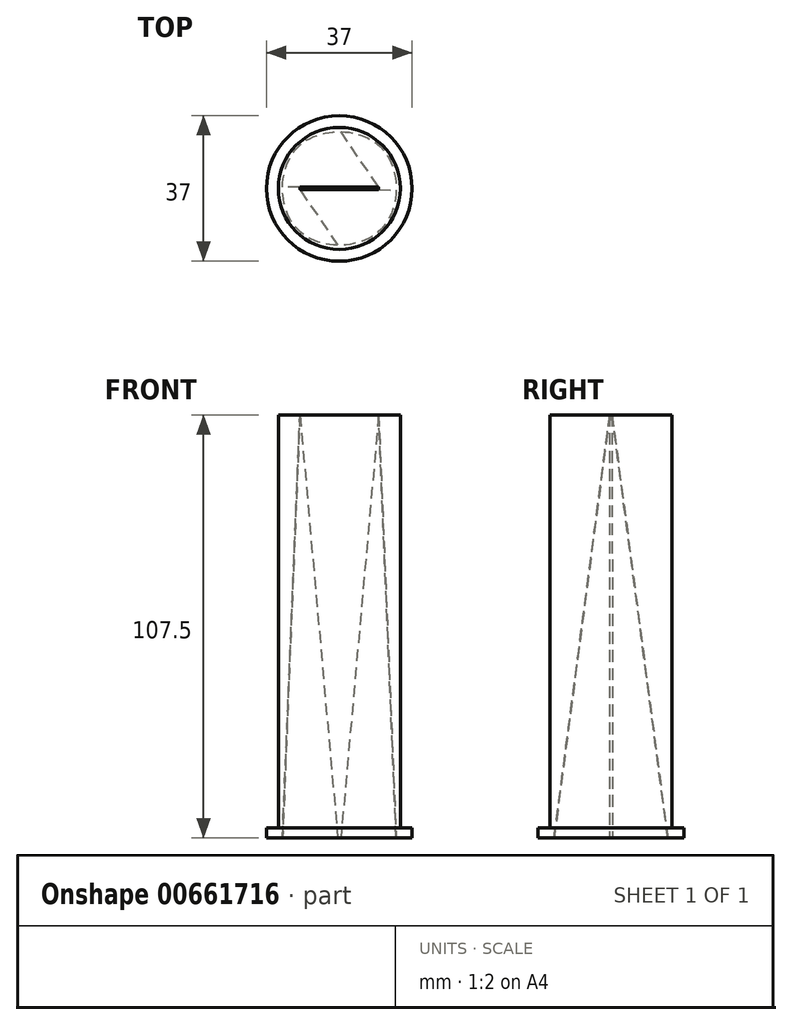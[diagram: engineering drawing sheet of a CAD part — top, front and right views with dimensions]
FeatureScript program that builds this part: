
annotation { "Feature Type Name" : "Feature", "Feature Type Description" : "" }
export const myFeature = defineFeature(function(context is Context, id is Id, definition is map)
    precondition{}
    {
        {
            var Q0;
            Q0=qCreatedBy(makeId("Top.planeOp"),FACE);
            var sketch = newSketch(context, id + "F0", { "sketchPlane" : qUnion([Q0])});
            skCircle(sketch, "E0", {"center": v(0, 0) * mm, "radius": 18.5 * mm});
            skSolve(sketch);
        }
        {
            var Q0;
            Q0=makeQuery(id+"F0.imprint","IMPRINT",FACE,{"disambiguationData":[TD([[makeQuery(id+"F0.imprint","IMPRINT",EDGE,{"derivedFrom":sQuery(id+"F0.wireOp",EDGE,"E0")}),1.0]])]});
            extrude(context, id + "F1", {"entities" : qUnion([Q0]), "depth" : 2.5 * mm, "offsetDistance" : 25 * mm});
        }
        {
            var Q0;
            Q0=makeQuery(id+"F1.opExtrude","CAP_FACE",FACE,{"disambiguationData":[OSD([sQuery(id+"F0.wireOp",EDGE,"E0")])],"isStart":false});
            var sketch = newSketch(context, id + "F2", { "sketchPlane" : qUnion([Q0])});
            skCircle(sketch, "E1", {"center": v(0, 0) * mm, "radius": 15.5 * mm});
            skSolve(sketch);
        }
        {
            var Q0;
            Q0 = qSketchRegion(id + "F2", true);
            extrude(context, id + "F3", {"entities" : qUnion([Q0]), "operationType" : NewBodyOperationType.ADD, "depth" : 105 * mm, "offsetDistance" : 25 * mm});
        }
        {
            var Q0;
            Q0=makeQuery(id+"F3.opExtrude","CAP_FACE",FACE,{"disambiguationData":[OSD([sQuery(id+"F2.wireOp",EDGE,"E1")])],"isStart":false});
            var sketch = newSketch(context, id + "F4", { "sketchPlane" : qUnion([Q0])});
            skLineSegment(sketch, "E2.bottom", {"start": v(-10, 0.3) * mm, "end": v(10, 0.3) * mm});
            skLineSegment(sketch, "E2.top", {"start": v(-10, -0.3) * mm, "end": v(10, -0.3) * mm});
            skLineSegment(sketch, "E2.left", {"start": v(-10, 0.3) * mm, "end": v(-10, -0.3) * mm});
            skLineSegment(sketch, "E2.right", {"start": v(10, 0.3) * mm, "end": v(10, -0.3) * mm});
            skPoint(sketch, "E2.middle", {"position": v(0, 0) * mm});
            skSolve(sketch);
        }
        {
            var Q0;
            Q0=makeQuery(id+"F1.opExtrude","CAP_FACE",FACE,{"disambiguationData":[OSD([sQuery(id+"F0.wireOp",EDGE,"E0")])],"isStart":true});
            var sketch = newSketch(context, id + "F5", { "sketchPlane" : qUnion([Q0])});
            skPoint(sketch, "E3.middle", {"position": v(0, 0) * mm});
            skFitSpline(sketch, "E4", {"points": [v(-10.5, 10.5) * mm, v(-10.5, -10.5) * mm, v(10.5, -10.5) * mm, v(10.5, 10.5) * mm, v(-10.5, 10.5) * mm]});
            skSolve(sketch);
        }
        {
            var Q1;
            Q1 = qSketchRegion(id + "F4", true);
            var Q2;
            Q2 = qSketchRegion(id + "F5", true);
            loft(context, id + "F6", {"operationType" : NewBodyOperationType.REMOVE, "sheetProfilesArray" : [{ "sheetProfileEntities" : qUnion([Q1]) }, { "sheetProfileEntities" : qUnion([Q2]) }]});
        }
    });
